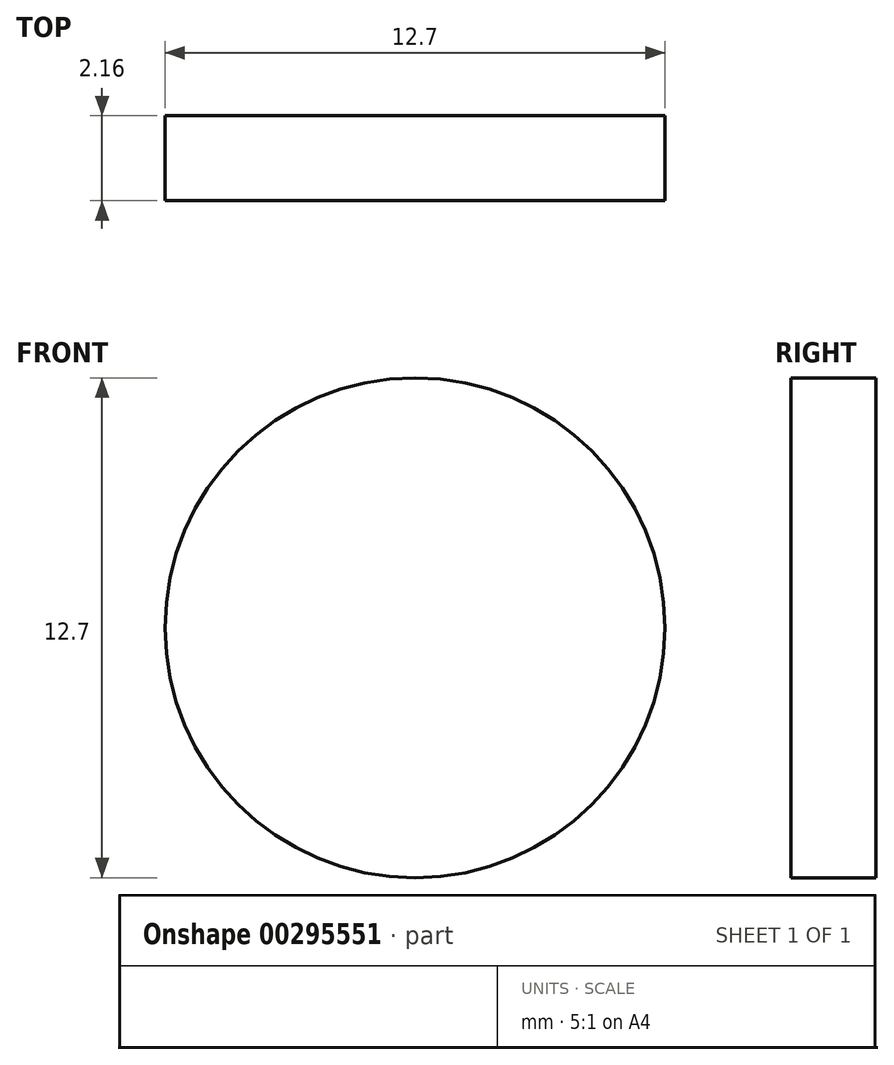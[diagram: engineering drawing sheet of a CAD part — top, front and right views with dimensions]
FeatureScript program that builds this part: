
annotation { "Feature Type Name" : "Feature", "Feature Type Description" : "" }
export const myFeature = defineFeature(function(context is Context, id is Id, definition is map)
    precondition{}
    {
        {
            var Q0;
            Q0=qCreatedBy(makeId("Front.planeOp"),FACE);
            var sketch = newSketch(context, id + "F0", { "sketchPlane" : qUnion([Q0])});
            skCircle(sketch, "E0", {"center": v(0, 0) * mm, "radius": 6.35 * mm});
            skSolve(sketch);
        }
        {
            var Q0;
            Q0 = qSketchRegion(id + "F0", true);
            extrude(context, id + "F1", {"entities" : qUnion([Q0]), "depth" : 2.16 * mm});
        }
    });
